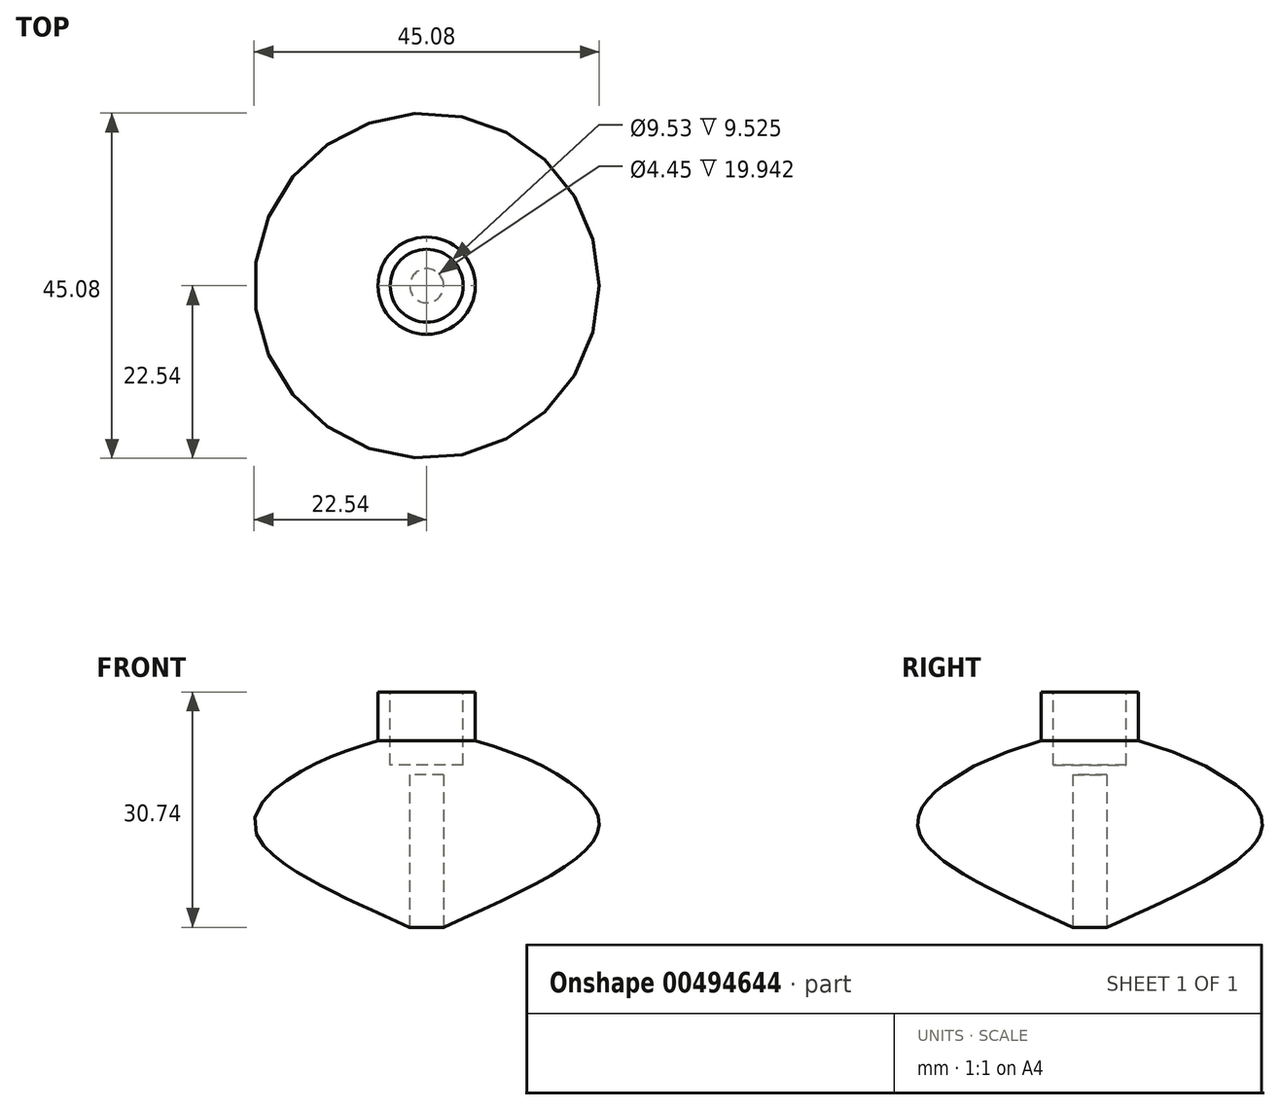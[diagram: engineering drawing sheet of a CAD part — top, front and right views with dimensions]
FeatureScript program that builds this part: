
annotation { "Feature Type Name" : "Feature", "Feature Type Description" : "" }
export const myFeature = defineFeature(function(context is Context, id is Id, definition is map)
    precondition{}
    {
        {
            var Q0;
            Q0=qCreatedBy(makeId("Front.planeOp"),FACE);
            var sketch = newSketch(context, id + "F0", { "sketchPlane" : qUnion([Q0])});
            skFitSpline(sketch, "E0", {"points": [v(0, 0) * mm, v(22.53, 14.4) * mm, v(6.35, 25.4) * mm], "startDerivative": vector(63.4, 29.07) * mm, "endDerivative": vector(-56.85, 15.94) * mm});
            skLineSegment(sketch, "E1", {"start": v(6.35, 25.4) * mm, "end": v(6.35, 31.75) * mm});
            skLineSegment(sketch, "E2", {"start": v(6.35, 31.75) * mm, "end": v(0, 31.75) * mm});
            skLineSegment(sketch, "E3", {"start": v(0, 31.75) * mm, "end": v(0, 0) * mm});
            skSolve(sketch);
        }
        {
            var Q0;
            Q0 = qSketchRegion(id + "F0", true);
            var Q1;
            Q1=sQuery(id+"F0.wireOp",EDGE,"E3");
            revolve(context, id + "F1", {"entities" : qUnion([Q0]), "axis" : qUnion([Q1]), "revolveType" : RevolveType.FULL});
        }
        {
            var Q0;
            Q0=makeQuery(id+"F1.opRevolve","SWEPT_FACE",FACE,{"disambiguationData":[OSD([sQuery(id+"F0.wireOp",EDGE,"E2")])]});
            var sketch = newSketch(context, id + "F2", { "sketchPlane" : qUnion([Q0])});
            skCircle(sketch, "E4", {"center": v(0, 0) * mm, "radius": 4.76 * mm});
            skSolve(sketch);
        }
        {
            var Q0;
            Q0=makeQuery(id+"F2.imprint","IMPRINT",FACE,{"disambiguationData":[TD([[makeQuery(id+"F2.imprint","IMPRINT",EDGE,{"derivedFrom":sQuery(id+"F2.wireOp",EDGE,"E4")}),1.0]])]});
            extrude(context, id + "F3", {"entities" : qUnion([Q0]), "operationType" : NewBodyOperationType.REMOVE, "oppositeDirection" : true, "depth" : 9.52 * mm});
        }
        {
            var Q0;
            Q0=qCreatedBy(makeId("Top.planeOp"),FACE);
            var sketch = newSketch(context, id + "F4", { "sketchPlane" : qUnion([Q0])});
            skCircle(sketch, "E5", {"center": v(0, 0) * mm, "radius": 2.22 * mm});
            skSolve(sketch);
        }
        {
            var Q0;
            Q0 = qSketchRegion(id + "F4", true);
            extrude(context, id + "F5", {"entities" : qUnion([Q0]), "operationType" : NewBodyOperationType.REMOVE, "depth" : 20.95 * mm});
        }
    });
